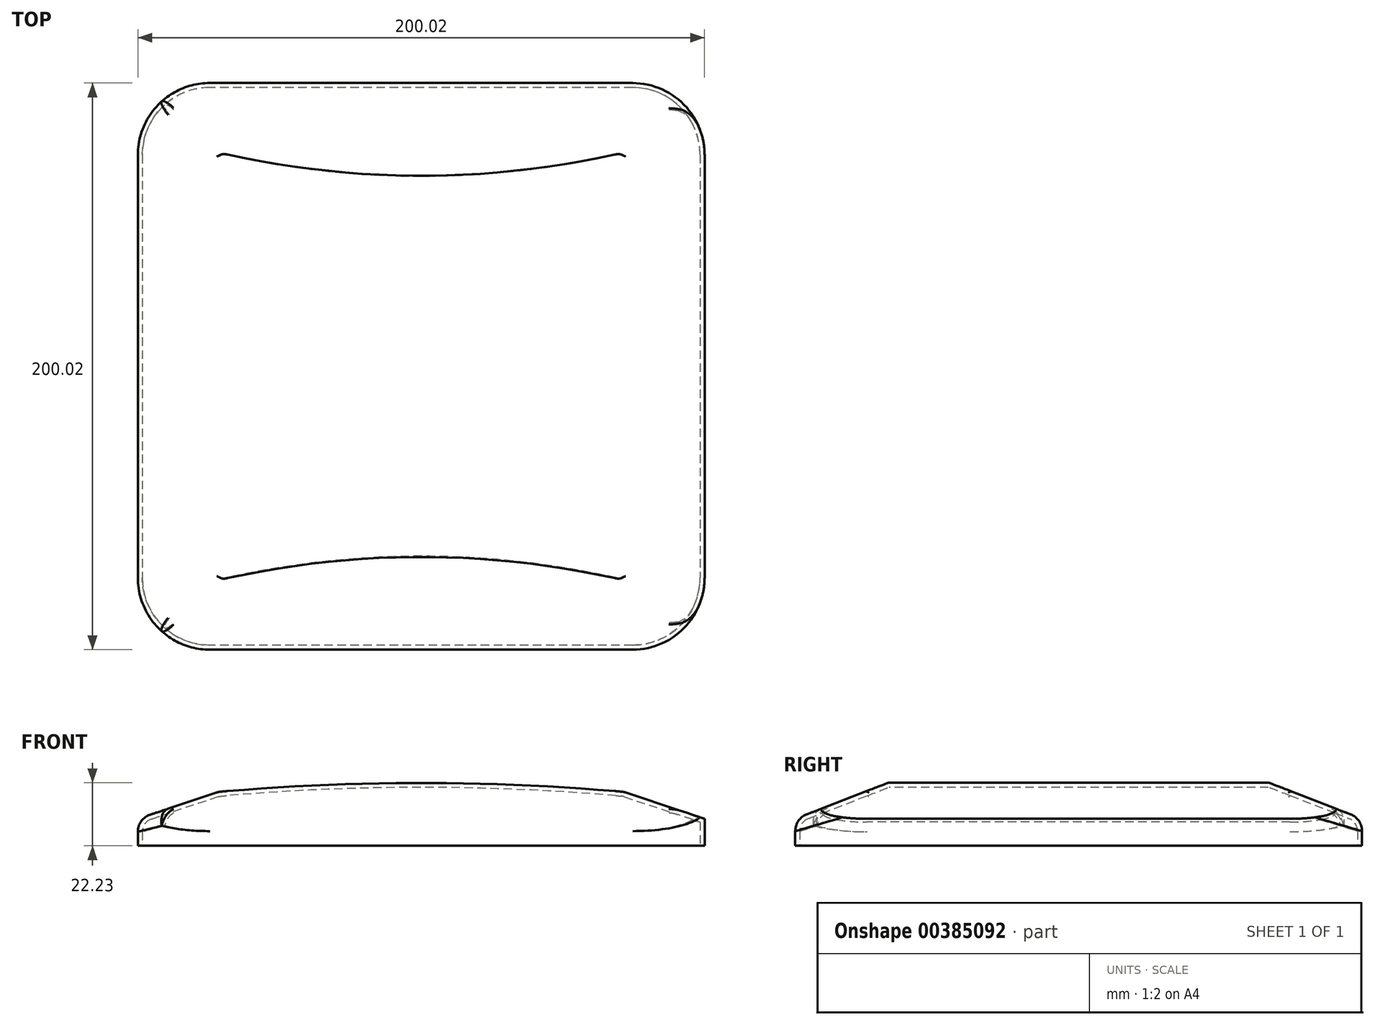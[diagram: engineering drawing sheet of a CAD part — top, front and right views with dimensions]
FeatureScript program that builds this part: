
annotation { "Feature Type Name" : "Feature", "Feature Type Description" : "" }
export const myFeature = defineFeature(function(context is Context, id is Id, definition is map)
    precondition{}
    {
        {
            var Q0;
            Q0=qCreatedBy(makeId("Top.planeOp"),FACE);
            var sketch = newSketch(context, id + "F0", { "sketchPlane" : qUnion([Q0])});
            skLineSegment(sketch, "E0.bottom", {"start": v(74.61, 100.01) * mm, "end": v(-74.61, 100.01) * mm});
            skLineSegment(sketch, "E0.top", {"start": v(74.61, -100.01) * mm, "end": v(-74.61, -100.01) * mm});
            skLineSegment(sketch, "E0.left", {"start": v(100.01, 74.61) * mm, "end": v(100.01, -74.61) * mm});
            skLineSegment(sketch, "E0.right", {"start": v(-100.01, 74.61) * mm, "end": v(-100.01, -74.61) * mm});
            skPoint(sketch, "E0.middle", {"position": v(0, 0) * mm});
            skPoint(sketch, "E1.visualSharp", {"position": v(-100.01, 100.01) * mm});
            skArc(sketch, "E1.filletArc", {"start": v(-74.61, 100.01) * mm, "mid": v(-92.57, 92.57) * mm, "end": v(-100.01, 74.61) * mm});
            skPoint(sketch, "E2.visualSharp", {"position": v(100.01, 100.01) * mm});
            skArc(sketch, "E2.filletArc", {"start": v(100.01, 74.61) * mm, "mid": v(92.57, 92.57) * mm, "end": v(74.61, 100.01) * mm});
            skPoint(sketch, "E3.visualSharp", {"position": v(100.01, -100.01) * mm});
            skArc(sketch, "E3.filletArc", {"start": v(74.61, -100.01) * mm, "mid": v(92.57, -92.57) * mm, "end": v(100.01, -74.61) * mm});
            skPoint(sketch, "E4.visualSharp", {"position": v(-100.01, -100.01) * mm});
            skArc(sketch, "E4.filletArc", {"start": v(-100.01, -74.61) * mm, "mid": v(-92.57, -92.57) * mm, "end": v(-74.61, -100.01) * mm});
            skSolve(sketch);
        }
        {
            var Q0;
            Q0=makeQuery(id+"F0.imprint","IMPRINT",FACE,{"disambiguationData":[TD([[makeQuery(id+"F0.imprint","IMPRINT",EDGE,{"derivedFrom":sQuery(id+"F0.wireOp",EDGE,"E0.bottom")}),1.0]])]});
            extrude(context, id + "F1", {"entities" : qUnion([Q0]), "depth" : 22.22 * mm});
        }
        {
            var Q0;
            Q0=qCreatedBy(makeId("Front.planeOp"),FACE);
            var sketch = newSketch(context, id + "F2", { "sketchPlane" : qUnion([Q0])});
            skPoint(sketch, "E5.0", {"position": v(0, 0) * mm});
            skPoint(sketch, "E6.0", {"position": v(100.01, 0) * mm});
            skLineSegment(sketch, "E7", {"start": v(71.7, 18.96) * mm, "end": v(98.4, 10.06) * mm});
            skPoint(sketch, "E8.MirrorP", {"position": v(-100.01, 0) * mm});
            skLineSegment(sketch, "E9.MirrorCS", {"start": v(-71.7, 18.96) * mm, "end": v(-98.4, 10.06) * mm});
            skArc(sketch, "E10", {"start": v(71.16, 19.07) * mm, "mid": v(0, 22.23) * mm, "end": v(-71.16, 19.07) * mm});
            skPoint(sketch, "E11.visualSharp", {"position": v(-100.01, 9.53) * mm});
            skPoint(sketch, "E12.visualSharp", {"position": v(100.01, 9.53) * mm});
            skPoint(sketch, "E13.visualSharp", {"position": v(71.44, 19.05) * mm});
            skPoint(sketch, "E14.visualSharp", {"position": v(-71.44, 19.05) * mm});
            skLineSegment(sketch, "E15.top", {"start": v(-100.01, 28.87) * mm, "end": v(100.01, 28.87) * mm});
            skLineSegment(sketch, "E15.left", {"start": v(-100.01, 9.53) * mm, "end": v(-100.01, 28.87) * mm});
            skLineSegment(sketch, "E15.right", {"start": v(100.01, 9.53) * mm, "end": v(100.01, 28.87) * mm});
            skLineSegment(sketch, "E16", {"start": v(0, 28.87) * mm, "end": v(0, 22.23) * mm});
            skLineSegment(sketch, "E17", {"start": v(-98.4, 10.06) * mm, "end": v(-100.01, 9.53) * mm});
            skLineSegment(sketch, "E18", {"start": v(-71.16, 19.07) * mm, "end": v(-71.44, 19.05) * mm});
            skLineSegment(sketch, "E19", {"start": v(-71.7, 18.96) * mm, "end": v(-71.44, 19.05) * mm});
            skLineSegment(sketch, "E20", {"start": v(71.7, 18.96) * mm, "end": v(71.44, 19.05) * mm});
            skLineSegment(sketch, "E21", {"start": v(71.44, 19.05) * mm, "end": v(71.16, 19.07) * mm});
            skLineSegment(sketch, "E22", {"start": v(100.01, 9.52) * mm, "end": v(98.4, 10.06) * mm});
            skPoint(sketch, "E12.filletArc.start.orphan", {"position": v(100.01, 7.82) * mm});
            skArc(sketch, "E23", {"start": v(71.44, 19.05) * mm, "mid": v(0, 22.23) * mm, "end": v(-71.44, 19.05) * mm});
            skSolve(sketch);
        }
        {
            var Q0;
            Q0 = qSketchRegion(id + "F2", true);
            extrude(context, id + "F3", {"entities" : qUnion([Q0]), "operationType" : NewBodyOperationType.REMOVE, "oppositeDirection" : true, "depth" : 228.6 * mm, "symmetric" : true});
        }
        {
            var Q0;
            Q0=qCreatedBy(makeId("Right.planeOp"),FACE);
            var sketch = newSketch(context, id + "F4", { "sketchPlane" : qUnion([Q0])});
            skLineSegment(sketch, "E24", {"start": v(-54.23, 27.28) * mm, "end": v(-100.01, 9.53) * mm});
            skLineSegment(sketch, "E25", {"start": v(-54.23, 27.28) * mm, "end": v(-103.24, 27.28) * mm});
            skLineSegment(sketch, "E26", {"start": v(-103.24, 7.68) * mm, "end": v(-100.01, 9.53) * mm});
            skLineSegment(sketch, "E27", {"start": v(-103.24, 7.68) * mm, "end": v(-103.24, 27.28) * mm});
            skLineSegment(sketch, "E28.MirrorCS", {"start": v(103.24, 7.68) * mm, "end": v(100.01, 9.53) * mm});
            skLineSegment(sketch, "E29.MirrorCS", {"start": v(54.23, 27.28) * mm, "end": v(100.01, 9.52) * mm});
            skLineSegment(sketch, "E30.MirrorCS", {"start": v(54.23, 27.28) * mm, "end": v(103.24, 27.28) * mm});
            skLineSegment(sketch, "E31.MirrorCS", {"start": v(103.24, 7.68) * mm, "end": v(103.24, 27.28) * mm});
            skSolve(sketch);
        }
        {
            var Q0;
            Q0=makeQuery(id+"F4.imprint","IMPRINT",FACE,{"disambiguationData":[TD([[makeQuery(id+"F4.imprint","IMPRINT",EDGE,{"derivedFrom":sQuery(id+"F4.wireOp",EDGE,"E24")}),-1.0]])]});
            var Q1;
            Q1=makeQuery(id+"F4.imprint","IMPRINT",FACE,{"disambiguationData":[TD([[makeQuery(id+"F4.imprint","IMPRINT",EDGE,{"derivedFrom":sQuery(id+"F4.wireOp",EDGE,"E28.MirrorCS")}),-1.0]])]});
            extrude(context, id + "F5", {"entities" : qUnion([Q0, Q1]), "operationType" : NewBodyOperationType.REMOVE, "oppositeDirection" : true, "depth" : 231.14 * mm, "symmetric" : true});
        }
        {
            var Q0;
            Q0=makeQuery(id+"F3.boolean.opBoolean","COPY",EDGE,{"derivedFrom":makeQuery(id+"F3.opExtrude","SWEPT_EDGE",EDGE,{"disambiguationData":[OSD([sQuery(id+"F2.wireOp",EDGE,"E15.right"),sQuery(id+"F2.wireOp",EDGE,"E22")])]})});
            var Q1;
            Q1=makeQuery(id+"F5.boolean.opBoolean","INTERSECT",EDGE,{"derivedFrom":[makeQuery(id+"F1.opExtrude","SWEPT_FACE",FACE,{"disambiguationData":[OSD([sQuery(id+"F0.wireOp",EDGE,"E2.filletArc")])]}),makeQuery(id+"F5.opExtrude","SWEPT_FACE",FACE,{"disambiguationData":[OSD([sQuery(id+"F4.wireOp",EDGE,"E29.MirrorCS")])]})]});
            var Q2;
            Q2=makeQuery(id+"F5.boolean.opBoolean","INTERSECT",EDGE,{"derivedFrom":[makeQuery(id+"F3.boolean.opBoolean","COPY",FACE,{"derivedFrom":makeQuery(id+"F3.opExtrude","SWEPT_FACE",FACE,{"disambiguationData":[OSD([sQuery(id+"F2.wireOp",EDGE,"E7"),sQuery(id+"F2.wireOp",EDGE,"E20"),sQuery(id+"F2.wireOp",EDGE,"E22")])]})}),makeQuery(id+"F5.opExtrude","SWEPT_FACE",FACE,{"disambiguationData":[OSD([sQuery(id+"F4.wireOp",EDGE,"E29.MirrorCS")])]})]});
            var Q3;
            Q3=makeQuery(id+"F5.boolean.opBoolean","INTERSECT",EDGE,{"derivedFrom":[makeQuery(id+"F3.boolean.opBoolean","COPY",FACE,{"derivedFrom":makeQuery(id+"F3.opExtrude","SWEPT_FACE",FACE,{"disambiguationData":[OSD([sQuery(id+"F2.wireOp",EDGE,"E23")])]})}),makeQuery(id+"F5.opExtrude","SWEPT_FACE",FACE,{"disambiguationData":[OSD([sQuery(id+"F4.wireOp",EDGE,"E29.MirrorCS")])]})]});
            var Q4;
            Q4=makeQuery(id+"F5.boolean.opBoolean","INTERSECT",EDGE,{"derivedFrom":[makeQuery(id+"F3.boolean.opBoolean","COPY",FACE,{"derivedFrom":makeQuery(id+"F3.opExtrude","SWEPT_FACE",FACE,{"disambiguationData":[OSD([sQuery(id+"F2.wireOp",EDGE,"E9.MirrorCS"),sQuery(id+"F2.wireOp",EDGE,"E17"),sQuery(id+"F2.wireOp",EDGE,"E19")])]})}),makeQuery(id+"F5.opExtrude","SWEPT_FACE",FACE,{"disambiguationData":[OSD([sQuery(id+"F4.wireOp",EDGE,"E29.MirrorCS")])]})]});
            var Q5;
            Q5=makeQuery(id+"F3.boolean.opBoolean","INTERSECT",EDGE,{"derivedFrom":[makeQuery(id+"F1.opExtrude","SWEPT_FACE",FACE,{"disambiguationData":[OSD([sQuery(id+"F0.wireOp",EDGE,"E1.filletArc")])]}),makeQuery(id+"F3.opExtrude","SWEPT_FACE",FACE,{"disambiguationData":[OSD([sQuery(id+"F2.wireOp",EDGE,"E9.MirrorCS"),sQuery(id+"F2.wireOp",EDGE,"E17"),sQuery(id+"F2.wireOp",EDGE,"E19")])]})]});
            var Q6;
            Q6=makeQuery(id+"F3.boolean.opBoolean","COPY",EDGE,{"derivedFrom":makeQuery(id+"F3.opExtrude","SWEPT_EDGE",EDGE,{"disambiguationData":[OSD([sQuery(id+"F2.wireOp",EDGE,"E15.left"),sQuery(id+"F2.wireOp",EDGE,"E17")])]})});
            var Q7;
            Q7=makeQuery(id+"F3.boolean.opBoolean","COPY",EDGE,{"derivedFrom":makeQuery(id+"F3.opExtrude","SWEPT_EDGE",EDGE,{"disambiguationData":[OSD([sQuery(id+"F2.wireOp",EDGE,"E19"),sQuery(id+"F2.wireOp",EDGE,"E23")])]})});
            var Q8;
            Q8=makeQuery(id+"F5.boolean.opBoolean","INTERSECT",EDGE,{"derivedFrom":[makeQuery(id+"F3.boolean.opBoolean","COPY",FACE,{"derivedFrom":makeQuery(id+"F3.opExtrude","SWEPT_FACE",FACE,{"disambiguationData":[OSD([sQuery(id+"F2.wireOp",EDGE,"E9.MirrorCS"),sQuery(id+"F2.wireOp",EDGE,"E17"),sQuery(id+"F2.wireOp",EDGE,"E19")])]})}),makeQuery(id+"F5.opExtrude","SWEPT_FACE",FACE,{"disambiguationData":[OSD([sQuery(id+"F4.wireOp",EDGE,"E24")])]})]});
            var Q9;
            Q9=makeQuery(id+"F5.boolean.opBoolean","INTERSECT",EDGE,{"derivedFrom":[makeQuery(id+"F3.boolean.opBoolean","COPY",FACE,{"derivedFrom":makeQuery(id+"F3.opExtrude","SWEPT_FACE",FACE,{"disambiguationData":[OSD([sQuery(id+"F2.wireOp",EDGE,"E23")])]})}),makeQuery(id+"F5.opExtrude","SWEPT_FACE",FACE,{"disambiguationData":[OSD([sQuery(id+"F4.wireOp",EDGE,"E24")])]})]});
            var Q10;
            Q10=makeQuery(id+"F5.boolean.opBoolean","INTERSECT",EDGE,{"derivedFrom":[makeQuery(id+"F1.opExtrude","SWEPT_FACE",FACE,{"disambiguationData":[OSD([sQuery(id+"F0.wireOp",EDGE,"E4.filletArc")])]}),makeQuery(id+"F5.opExtrude","SWEPT_FACE",FACE,{"disambiguationData":[OSD([sQuery(id+"F4.wireOp",EDGE,"E24")])]})]});
            var Q11;
            Q11=makeQuery(id+"F5.boolean.opBoolean","COPY",EDGE,{"derivedFrom":makeQuery(id+"F5.opExtrude","SWEPT_EDGE",EDGE,{"disambiguationData":[OSD([sQuery(id+"F4.wireOp",EDGE,"E24"),sQuery(id+"F4.wireOp",EDGE,"E26")])]})});
            var Q12;
            Q12=makeQuery(id+"F5.boolean.opBoolean","INTERSECT",EDGE,{"derivedFrom":[makeQuery(id+"F3.boolean.opBoolean","COPY",FACE,{"derivedFrom":makeQuery(id+"F3.opExtrude","SWEPT_FACE",FACE,{"disambiguationData":[OSD([sQuery(id+"F2.wireOp",EDGE,"E7"),sQuery(id+"F2.wireOp",EDGE,"E20"),sQuery(id+"F2.wireOp",EDGE,"E22")])]})}),makeQuery(id+"F5.opExtrude","SWEPT_FACE",FACE,{"disambiguationData":[OSD([sQuery(id+"F4.wireOp",EDGE,"E24")])]})]});
            var Q13;
            Q13=makeQuery(id+"F3.boolean.opBoolean","COPY",EDGE,{"derivedFrom":makeQuery(id+"F3.opExtrude","SWEPT_EDGE",EDGE,{"disambiguationData":[OSD([sQuery(id+"F2.wireOp",EDGE,"E20"),sQuery(id+"F2.wireOp",EDGE,"E23")])]})});
            fillet(context, id + "F6", {"entities" : qUnion([Q0, Q1, Q2, Q3, Q4, Q5, Q6, Q7, Q8, Q9, Q10, Q11, Q12, Q13]), "radius" : 6.35 * mm, "tangentPropagation" : true, "allowEdgeOverflow" : false});
        }
        {
            var Q0;
            Q0=makeQuery(id+"F1.opExtrude","CAP_FACE",FACE,{"disambiguationData":[OSD([sQuery(id+"F0.wireOp",EDGE,"E0.bottom"),sQuery(id+"F0.wireOp",EDGE,"E0.top"),sQuery(id+"F0.wireOp",EDGE,"E0.left"),sQuery(id+"F0.wireOp",EDGE,"E0.right"),sQuery(id+"F0.wireOp",EDGE,"E1.filletArc"),sQuery(id+"F0.wireOp",EDGE,"E2.filletArc"),sQuery(id+"F0.wireOp",EDGE,"E3.filletArc"),sQuery(id+"F0.wireOp",EDGE,"E4.filletArc")])],"isStart":true});
            shell(context, id + "F7", {"entities" : qUnion([Q0]), "thickness" : 1.59 * mm});
        }
    });
